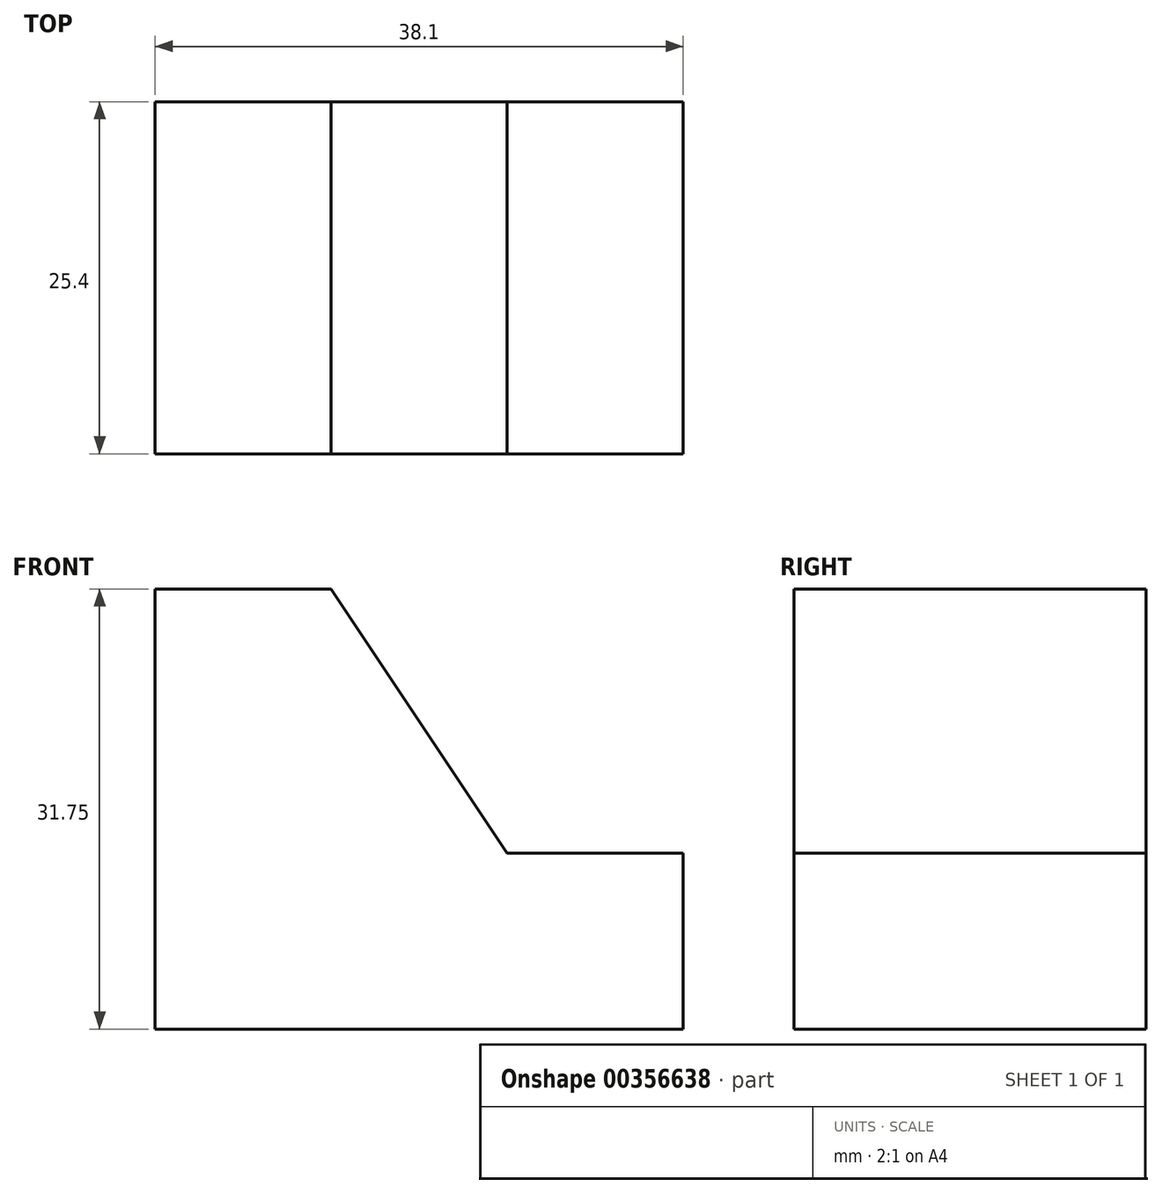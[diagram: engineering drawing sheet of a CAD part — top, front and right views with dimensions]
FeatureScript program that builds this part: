
annotation { "Feature Type Name" : "Feature", "Feature Type Description" : "" }
export const myFeature = defineFeature(function(context is Context, id is Id, definition is map)
    precondition{}
    {
        {
            var Q0;
            Q0=qCreatedBy(makeId("Front.planeOp"),FACE);
            var sketch = newSketch(context, id + "F0", { "sketchPlane" : qUnion([Q0])});
            skLineSegment(sketch, "E0", {"start": v(-38.1, 31.75) * mm, "end": v(0, 31.75) * mm});
            skLineSegment(sketch, "E1", {"start": v(0, 31.75) * mm, "end": v(0, 0) * mm});
            skLineSegment(sketch, "E2", {"start": v(0, 0) * mm, "end": v(-38.1, 0) * mm});
            skLineSegment(sketch, "E3", {"start": v(-38.1, 0) * mm, "end": v(-38.1, 31.75) * mm});
            skSolve(sketch);
        }
        {
            var Q0;
            Q0 = qSketchRegion(id + "F0", true);
            extrude(context, id + "F1", {"entities" : qUnion([Q0]), "depth" : 25.4 * mm});
        }
        {
            var Q0;
            Q0=makeQuery(id+"F1.opExtrude","CAP_FACE",FACE,{"disambiguationData":[OSD([sQuery(id+"F0.wireOp",EDGE,"E0"),sQuery(id+"F0.wireOp",EDGE,"E1"),sQuery(id+"F0.wireOp",EDGE,"E2"),sQuery(id+"F0.wireOp",EDGE,"E3")])],"isStart":false});
            var sketch = newSketch(context, id + "F2", { "sketchPlane" : qUnion([Q0])});
            skLineSegment(sketch, "E4", {"start": v(0, 12.7) * mm, "end": v(-12.7, 12.7) * mm});
            skLineSegment(sketch, "E5", {"start": v(-12.7, 12.7) * mm, "end": v(-25.4, 31.75) * mm});
            skLineSegment(sketch, "E6", {"start": v(0, 12.7) * mm, "end": v(0, 0) * mm});
            skLineSegment(sketch, "E7", {"start": v(-12.7, 12.7) * mm, "end": v(-25.4, 12.7) * mm});
            skLineSegment(sketch, "E8", {"start": v(-25.4, 12.7) * mm, "end": v(-25.4, 31.75) * mm});
            skLineSegment(sketch, "E9", {"start": v(-25.4, 31.75) * mm, "end": v(0, 31.75) * mm});
            skLineSegment(sketch, "E10", {"start": v(0, 31.75) * mm, "end": v(0, 12.7) * mm});
            skSolve(sketch);
        }
        {
            var Q0;
            Q0=makeQuery(id+"F2.imprint","IMPRINT",FACE,{"disambiguationData":[TD([[makeQuery(id+"F2.imprint","IMPRINT",EDGE,{"derivedFrom":sQuery(id+"F2.wireOp",EDGE,"E4")}),-1.0]])]});
            extrude(context, id + "F3", {"entities" : qUnion([Q0]), "operationType" : NewBodyOperationType.REMOVE, "oppositeDirection" : true, "depth" : 25.4 * mm});
        }
    });
